# Revit family: DAL_A3-ExtSgl-(7)
name_source: partatom
category: Doors
revit_build: Autodesk Revit 2016 (Build: 20150220_1215(x64)
units: mm (PartAtom-declared; Revit-internal decimal feet)

## family parameters
Always vertical = Yes
Cut with Voids When Loaded = No
Host = Wall
Room Calculation Point = No
Shared = No

## types (3) — shared parameters
Cavity Closer Depth = 75 mm
Cavity Closer Offset from Ext = 102.5 mm  [stored 0.336286 ft]
Cavity Closer Width = 50 mm  [stored 0.164042 ft]
Cill Extension = 25 mm  [stored 0.082021 ft]
Cill Projection = 30 mm  [stored 0.0984252 ft]
Cill Thickness = 54.5 mm  [stored 0.178806 ft]
Door Panel Height = 2000 mm  [stored 6.56168 ft]
Door Panel Thickness = 44 mm  [stored 0.144357 ft]
FrameDepth = 89 mm  [stored 0.291995 ft]
FrameOffset - External = 25 mm  [stored 0.082021 ft]
FrameWidth = 42 mm  [stored 0.137795 ft]
Function = Interior
Glazing Thickness = 24 mm  [stored 0.0787402 ft]
Handle X Distance = 60 mm  [stored 0.19685 ft]
Handle Z Distance = 950 mm  [stored 3.1168 ft]
Height = 2110 mm  [stored 6.92257 ft]
Keynote = L20
Material Door = Door - Panel
Material Frame = Door -  Frame/Mullion
Material Glass = Door - Glazing
Material Ironmongery = Door - Handle
O/A Frame Width = 64 mm  [stored 0.209974 ft]
Operation = SingleSwingRight
Rough Height = 2110 mm  [stored 6.92257 ft]
Stile Bottom Rail = 175 mm  [stored 0.574147 ft]
Stile Hanging = 100 mm  [stored 0.328084 ft]
Stile Lock Rail = 150 mm
Stile Muntin Rail = 100 mm  [stored 0.328084 ft]
Stile Shutting = 100 mm  [stored 0.328084 ft]
Stile Top Rail = 150 mm
Stile Top of Lock rail = 1000 mm  [stored 3.28084 ft]
Structural Tolerance = 6.5 mm
Thickness = 44 mm  [stored 0.144357 ft]
Tolerance = 3 mm  [stored 0.00984252 ft]
Undercut = 4 mm  [stored 0.0131234 ft]
Vis - Cavity Closers = Yes
Vis - Ironmongery = Yes
Wall Closure = By host
Wrap Layers (Ext) from Ext = 102.5 mm  [stored 0.336286 ft]
Wrap Layers (Int) from Ext = 177.5 mm

## per-type parameters (varying)
| type | Door Panel Width | Rough Width | Width |
| 910 x 2110mm | 807 mm | 910 mm  [stored 2.98556 ft] | 910 mm  [stored 2.98556 ft] |
| 810 x 2110mm | 707 mm | 810 mm | 810 mm |
| 1010 x 2110mm | 907 mm  [stored 2.97572 ft] | 1010 mm  [stored 3.31365 ft] | 1010 mm  [stored 3.31365 ft] |

note: [stored X ft] marks values corroborated as IEEE doubles in the binary element streams (Revit-internal decimal feet)

## geometry (parser evidence)
native form markers: Sweep x4
no freeform markers — native parametric forms only
